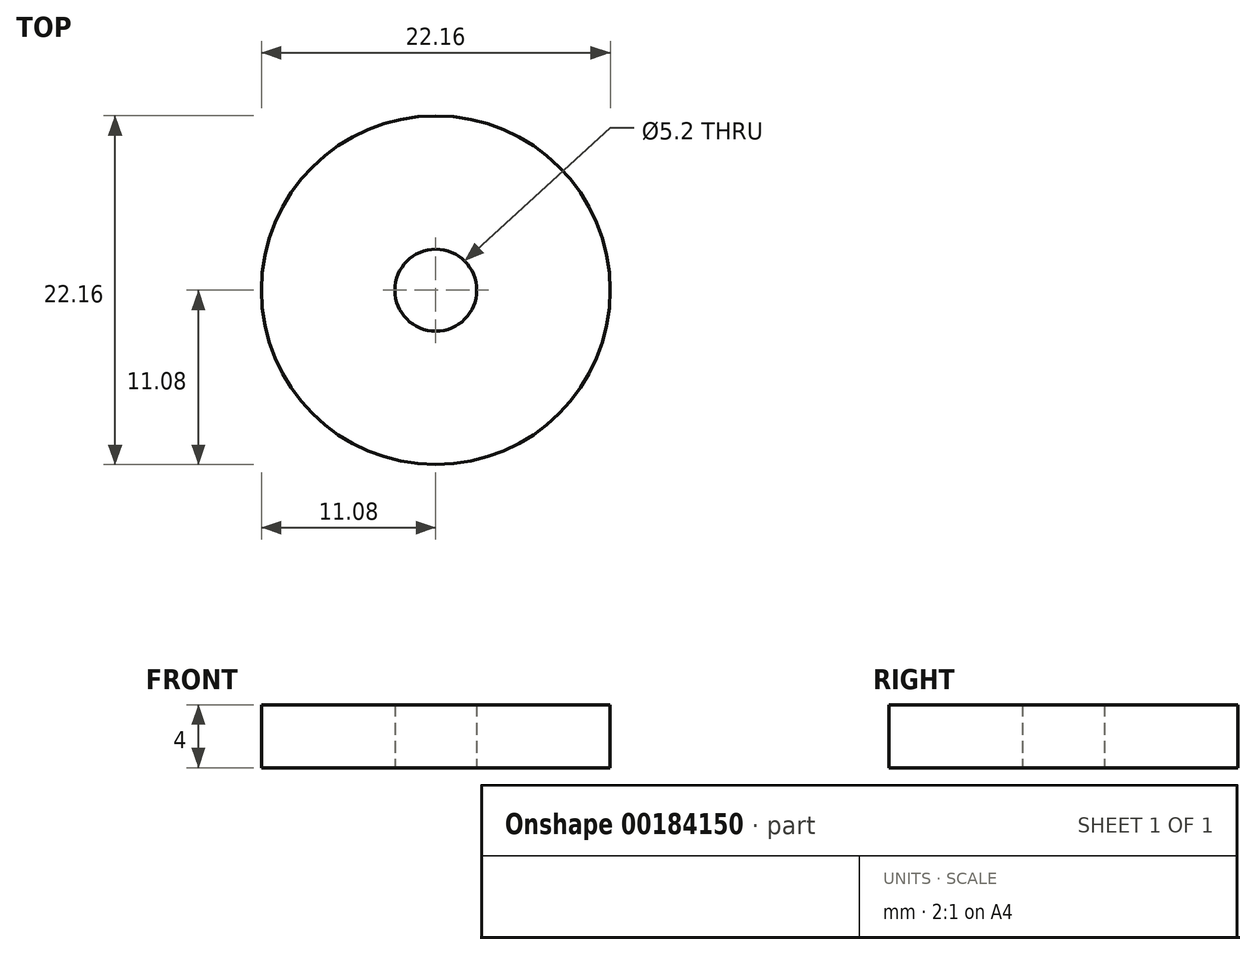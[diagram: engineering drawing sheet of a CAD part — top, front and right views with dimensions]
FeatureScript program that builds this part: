
annotation { "Feature Type Name" : "Feature", "Feature Type Description" : "" }
export const myFeature = defineFeature(function(context is Context, id is Id, definition is map)
    precondition{}
    {
        {
            var Q0;
            Q0=qCreatedBy(makeId("Top.planeOp"),FACE);
            var sketch = newSketch(context, id + "F0", { "sketchPlane" : qUnion([Q0])});
            skCircle(sketch, "E0", {"center": v(0, 0) * mm, "radius": 2.6 * mm});
            skCircle(sketch, "E1", {"center": v(0, 0) * mm, "radius": 11.07 * mm});
            skSolve(sketch);
        }
        {
            var Q0;
            Q0 = qSketchRegion(id + "F0", true);
            extrude(context, id + "F1", {"entities" : qUnion([Q0]), "depth" : 4 * mm});
        }
    });
